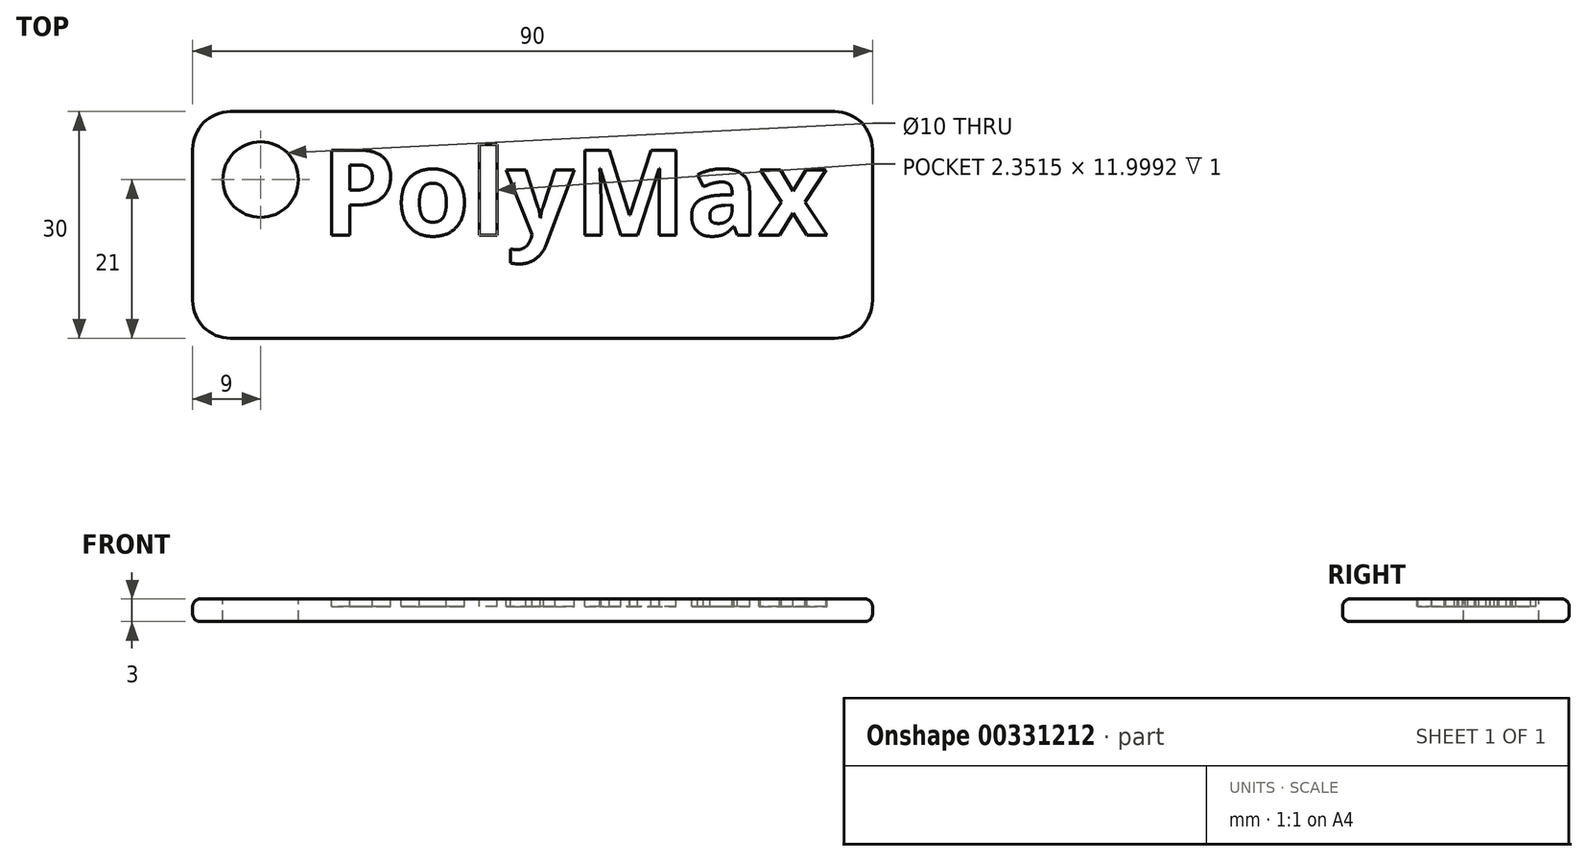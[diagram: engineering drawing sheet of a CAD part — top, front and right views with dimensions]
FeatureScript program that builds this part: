
annotation { "Feature Type Name" : "Feature", "Feature Type Description" : "" }
export const myFeature = defineFeature(function(context is Context, id is Id, definition is map)
    precondition{}
    {
        {
            var Q0;
            Q0=qCreatedBy(makeId("Top.planeOp"),FACE);
            var sketch = newSketch(context, id + "F0", { "sketchPlane" : qUnion([Q0])});
            skLineSegment(sketch, "E0.bottom", {"start": v(-45, 15) * mm, "end": v(45, 15) * mm});
            skLineSegment(sketch, "E0.top", {"start": v(-45, -15) * mm, "end": v(45, -15) * mm});
            skLineSegment(sketch, "E0.left", {"start": v(-45, 15) * mm, "end": v(-45, -15) * mm});
            skLineSegment(sketch, "E0.right", {"start": v(45, 15) * mm, "end": v(45, -15) * mm});
            skLineSegment(sketch, "E1", {"start": v(-45, 15) * mm, "end": v(45, -15) * mm, "construction": true});
            skSolve(sketch);
        }
        {
            var Q0;
            Q0=makeQuery(id+"F0.imprint","IMPRINT",FACE,{"disambiguationData":[TD([[makeQuery(id+"F0.imprint","IMPRINT",EDGE,{"derivedFrom":sQuery(id+"F0.wireOp",EDGE,"E0.bottom")}),-1.0]])]});
            extrude(context, id + "F1", {"entities" : qUnion([Q0]), "depth" : 3 * mm});
        }
        {
            var Q0;
            Q0=makeQuery(id+"F1.opExtrude","CAP_FACE",FACE,{"disambiguationData":[OSD([sQuery(id+"F0.wireOp",EDGE,"E0.bottom"),sQuery(id+"F0.wireOp",EDGE,"E0.top"),sQuery(id+"F0.wireOp",EDGE,"E0.left"),sQuery(id+"F0.wireOp",EDGE,"E0.right")])],"isStart":false});
            var Q1;
            Q1=makeQuery(id+"F1.opExtrude","CAP_FACE",FACE,{"disambiguationData":[OSD([sQuery(id+"F0.wireOp",EDGE,"E0.bottom"),sQuery(id+"F0.wireOp",EDGE,"E0.top"),sQuery(id+"F0.wireOp",EDGE,"E0.left"),sQuery(id+"F0.wireOp",EDGE,"E0.right")])],"isStart":true});
            fillet(context, id + "F2", {"entities" : qUnion([Q0, Q1]), "radius" : 1 * mm, "tangentPropagation" : true, "allowEdgeOverflow" : false});
        }
        {
            var Q0;
            Q0=makeQuery(id+"F1.opExtrude","SWEPT_EDGE",EDGE,{"disambiguationData":[OSD([sQuery(id+"F0.wireOp",EDGE,"E0.top"),sQuery(id+"F0.wireOp",EDGE,"E0.right")])]});
            var Q1;
            Q1=makeQuery(id+"F1.opExtrude","SWEPT_EDGE",EDGE,{"disambiguationData":[OSD([sQuery(id+"F0.wireOp",EDGE,"E0.bottom"),sQuery(id+"F0.wireOp",EDGE,"E0.right")])]});
            var Q2;
            Q2=makeQuery(id+"F1.opExtrude","SWEPT_EDGE",EDGE,{"disambiguationData":[OSD([sQuery(id+"F0.wireOp",EDGE,"E0.bottom"),sQuery(id+"F0.wireOp",EDGE,"E0.left")])]});
            var Q3;
            Q3=makeQuery(id+"F1.opExtrude","SWEPT_EDGE",EDGE,{"disambiguationData":[OSD([sQuery(id+"F0.wireOp",EDGE,"E0.top"),sQuery(id+"F0.wireOp",EDGE,"E0.left")])]});
            fillet(context, id + "F3", {"entities" : qUnion([Q0, Q1, Q2, Q3]), "radius" : 5 * mm, "tangentPropagation" : true, "allowEdgeOverflow" : false});
        }
        {
            var Q0;
            {var subQ0=sQuery(id+"F0.wireOp",EDGE,"E0.left");var subQ2=sQuery(id+"F0.wireOp",EDGE,"E0.bottom");var subQ4=sQuery(id+"F0.wireOp",EDGE,"E0.right");var subQ6=sQuery(id+"F0.wireOp",EDGE,"E0.top");Q0=makeQuery(id+"FmQCBBX3Ub0qneL_1.boolean.opBoolean","SPLIT",FACE,{"disambiguationData":[TD([makeQuery(id+"FmQCBBX3Ub0qneL_1.opExtrude","SWEPT_FACE",FACE,{"disambiguationData":[OSD([sQuery(id+"FOCoeRmDbjhRCuz_1.wireOp",EDGE,"4a1fb44a-e7be-4e23-9449-000d953c446c.sketch_text.stroke-0")])]})])],"derivedFrom":makeQuery(id+"F1.opExtrude","CAP_FACE",FACE,{"disambiguationData":[OSD([subQ2,subQ6,subQ0,subQ4])],"isStart":false})});}
            var sketch = newSketch(context, id + "F4", { "sketchPlane" : qUnion([Q0])});
            skCircle(sketch, "E2", {"center": v(-36, 6) * mm, "radius": 5 * mm});
            skSolve(sketch);
        }
        {
            var Q0;
            Q0=qSketchRegion(id+"F4",true);
            extrude(context, id + "F5", {"entities" : qUnion([Q0]), "operationType" : NewBodyOperationType.REMOVE, "oppositeDirection" : true, "depth" : 3 * mm});
        }
        {
            var Q0;
            Q0=makeQuery(id+"F1.opExtrude","CAP_FACE",FACE,{"disambiguationData":[OSD([sQuery(id+"F0.wireOp",EDGE,"E0.bottom"),sQuery(id+"F0.wireOp",EDGE,"E0.top"),sQuery(id+"F0.wireOp",EDGE,"E0.left"),sQuery(id+"F0.wireOp",EDGE,"E0.right")])],"isStart":false});
            var sketch = newSketch(context, id + "F6", { "sketchPlane" : qUnion([Q0])});
            skText(sketch, "E3", { "text": "PolyMax", "fontName": "OpenSans-Bold.ttf"});
            const initialGuessF6  = {"E3": [-0.028, -0.00137, 1, 0, 0.01137]};
            skSetInitialGuess(sketch, initialGuessF6);
            skSolve(sketch);
        }
        {
            var Q0;
            Q0=qSketchRegion(id+"F6",true);
            extrude(context, id + "F7", {"entities" : qUnion([Q0]), "operationType" : NewBodyOperationType.REMOVE, "oppositeDirection" : true, "depth" : 1 * mm});
        }
    });
